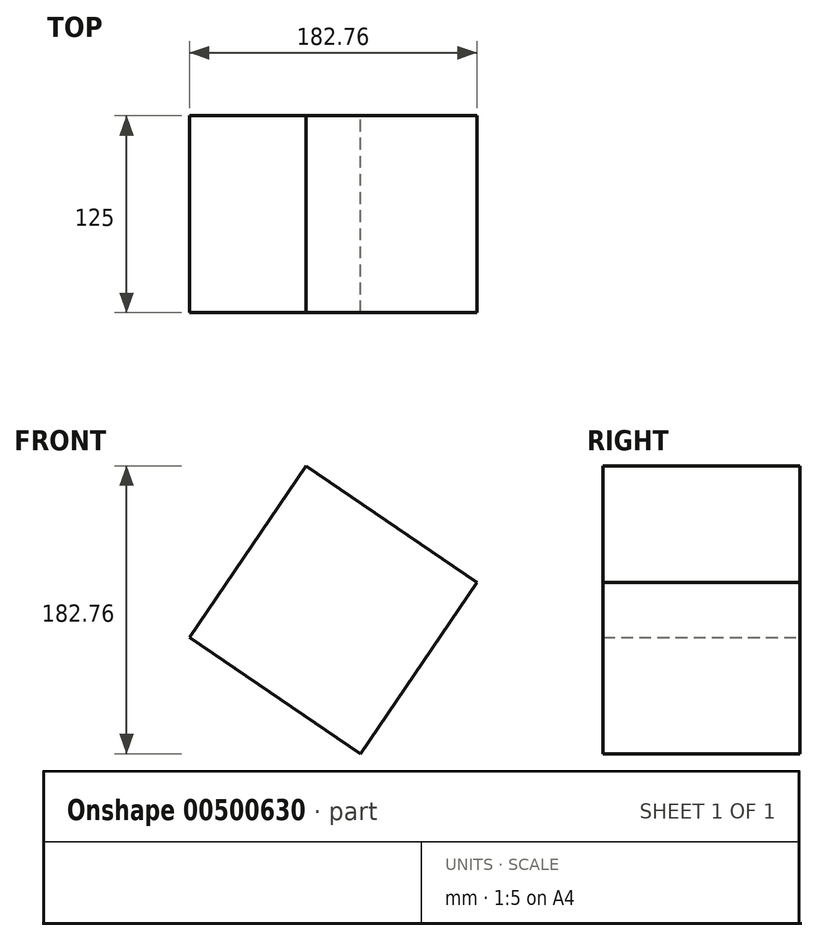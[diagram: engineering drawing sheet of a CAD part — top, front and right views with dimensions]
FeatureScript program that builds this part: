
annotation { "Feature Type Name" : "Feature", "Feature Type Description" : "" }
export const myFeature = defineFeature(function(context is Context, id is Id, definition is map)
    precondition{}
    {
        {
            var Q0;
            Q0=qCreatedBy(makeId("Front.planeOp"),FACE);
            var sketch = newSketch(context, id + "F0", { "sketchPlane" : qUnion([Q0])});
            skCircle(sketch, "E0.cCircle", {"center": v(2.04, 0) * mm, "radius": 65.77 * mm, "construction": true});
            skLineSegment(sketch, "E0.0", {"start": v(-15.3, 91.38) * mm, "end": v(93.42, 17.34) * mm});
            skLineSegment(sketch, "E0.1", {"start": v(93.42, 17.34) * mm, "end": v(19.38, -91.38) * mm});
            skLineSegment(sketch, "E0.2", {"start": v(19.38, -91.38) * mm, "end": v(-89.34, -17.34) * mm});
            skLineSegment(sketch, "E0.3", {"start": v(-89.34, -17.34) * mm, "end": v(-15.3, 91.38) * mm});
            skPoint(sketch, "E0.0.midPoint", {"position": v(39.06, 54.36) * mm});
            skSolve(sketch);
        }
        {
            var Q0;
            Q0=makeQuery(id+"F0.imprint","IMPRINT",FACE,{"disambiguationData":[TD([[makeQuery(id+"F0.imprint","IMPRINT",EDGE,{"derivedFrom":sQuery(id+"F0.wireOp",EDGE,"E0.0")}),-1.0]])]});
            extrude(context, id + "F1", {"entities" : qUnion([Q0]), "depth" : 125 * mm});
        }
    });
